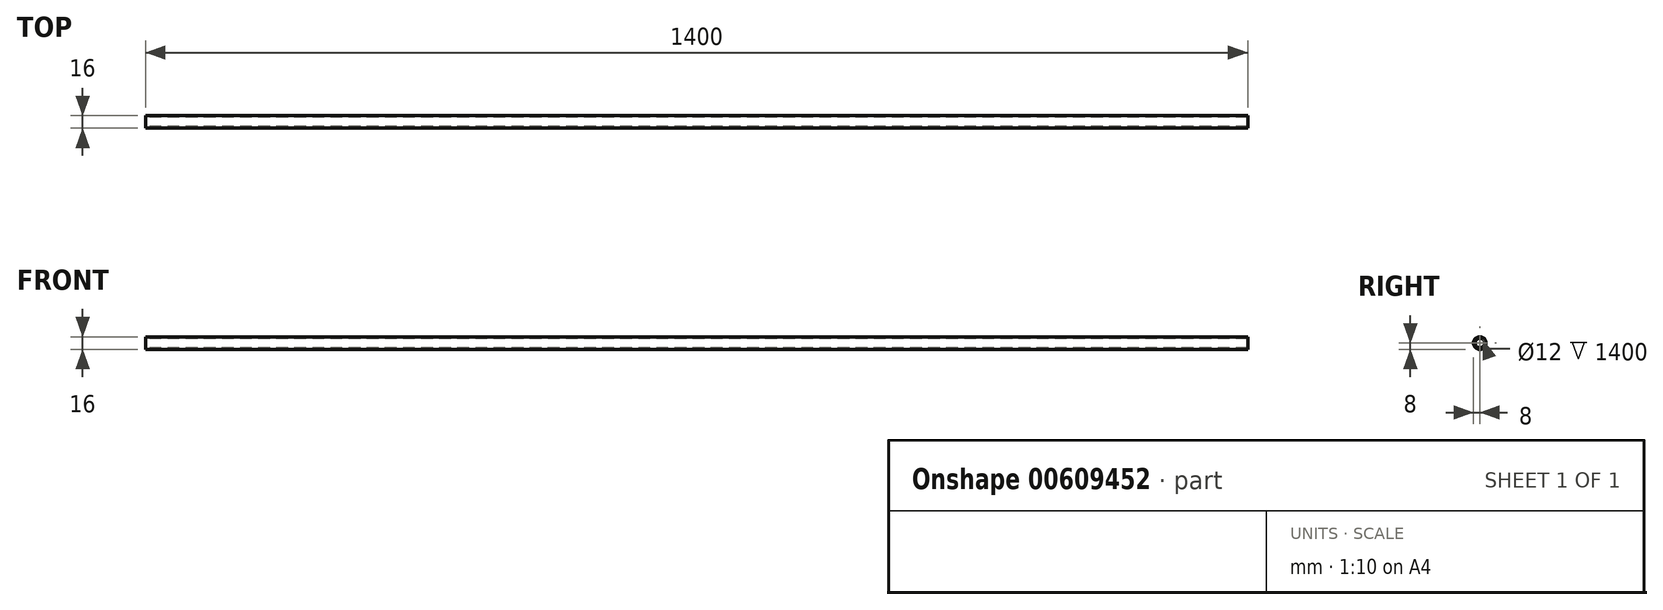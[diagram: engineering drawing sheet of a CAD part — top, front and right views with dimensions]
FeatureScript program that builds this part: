
annotation { "Feature Type Name" : "Feature", "Feature Type Description" : "" }
export const myFeature = defineFeature(function(context is Context, id is Id, definition is map)
    precondition{}
    {
        {
            var Q0;
            Q0=qCreatedBy(makeId("Right.planeOp"),FACE);
            var sketch = newSketch(context, id + "F0", { "sketchPlane" : qUnion([Q0])});
            skCircle(sketch, "E0", {"center": v(0, 0) * mm, "radius": 8 * mm});
            skCircle(sketch, "E1", {"center": v(0, 0) * mm, "radius": 6 * mm});
            skSolve(sketch);
        }
        {
            var Q0;
            Q0=makeQuery(id+"F0.imprint","IMPRINT",FACE,{"disambiguationData":[TD([[makeQuery(id+"F0.imprint","IMPRINT",EDGE,{"derivedFrom":sQuery(id+"F0.wireOp",EDGE,"E0")}),1.0]])]});
            extrude(context, id + "F1", {"entities" : qUnion([Q0]), "depth" : 1400 * mm, "offsetDistance" : 25.4 * mm});
        }
    });
